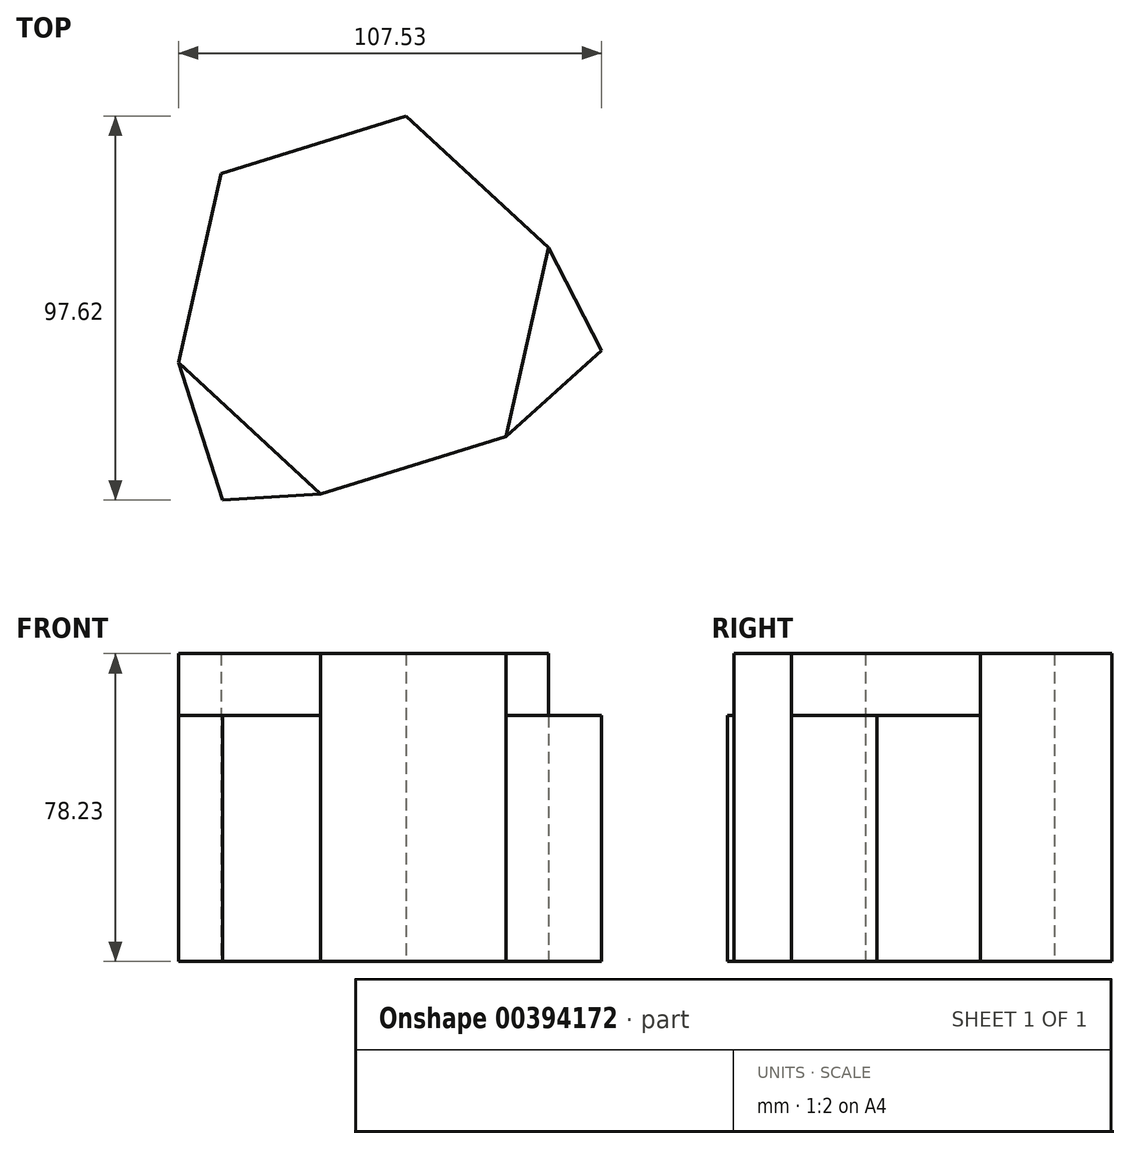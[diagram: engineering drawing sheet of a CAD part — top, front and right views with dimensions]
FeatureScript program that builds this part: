
annotation { "Feature Type Name" : "Feature", "Feature Type Description" : "" }
export const myFeature = defineFeature(function(context is Context, id is Id, definition is map)
    precondition{}
    {
        {
            var Q0;
            Q0=qCreatedBy(makeId("Top.planeOp"),FACE);
            var sketch = newSketch(context, id + "F0", { "sketchPlane" : qUnion([Q0])});
            skCircle(sketch, "E0.cCircle", {"center": v(0, 0) * mm, "radius": 42.64 * mm, "construction": true});
            skLineSegment(sketch, "E0.0", {"start": v(-47.01, -14.63) * mm, "end": v(-36.18, 33.4) * mm});
            skLineSegment(sketch, "E0.1", {"start": v(-36.18, 33.4) * mm, "end": v(10.83, 48.03) * mm});
            skLineSegment(sketch, "E0.2", {"start": v(10.83, 48.03) * mm, "end": v(47.01, 14.63) * mm});
            skLineSegment(sketch, "E0.3", {"start": v(47.01, 14.63) * mm, "end": v(36.18, -33.4) * mm});
            skLineSegment(sketch, "E0.4", {"start": v(36.18, -33.4) * mm, "end": v(-10.83, -48.03) * mm});
            skLineSegment(sketch, "E0.5", {"start": v(-10.83, -48.03) * mm, "end": v(-47.01, -14.63) * mm});
            skPoint(sketch, "E0.0.midPoint", {"position": v(-41.6, 9.38) * mm});
            skLineSegment(sketch, "E1", {"start": v(-47.01, -14.63) * mm, "end": v(-35.83, -49.59) * mm});
            skLineSegment(sketch, "E2", {"start": v(-35.83, -49.59) * mm, "end": v(-10.83, -48.03) * mm});
            skLineSegment(sketch, "E3", {"start": v(36.18, -33.4) * mm, "end": v(60.52, -11.59) * mm});
            skLineSegment(sketch, "E4", {"start": v(60.52, -11.59) * mm, "end": v(47.01, 14.63) * mm});
            skSolve(sketch);
        }
        {
            var Q0;
            Q0=makeQuery(id+"F0.imprint","IMPRINT",FACE,{"disambiguationData":[TD([[makeQuery(id+"F0.imprint","IMPRINT",EDGE,{"derivedFrom":sQuery(id+"F0.wireOp",EDGE,"E0.0")}),-1.0]])]});
            extrude(context, id + "F1", {"entities" : qUnion([Q0]), "depth" : 78.23 * mm});
        }
        {
            var Q0;
            Q0=makeQuery(id+"F0.imprint","IMPRINT",FACE,{"disambiguationData":[TD([[makeQuery(id+"F0.imprint","IMPRINT",EDGE,{"derivedFrom":sQuery(id+"F0.wireOp",EDGE,"E0.5")}),1.0]])]});
            extrude(context, id + "F2", {"entities" : qUnion([Q0]), "operationType" : NewBodyOperationType.ADD, "depth" : 62.48 * mm});
        }
        {
            var Q0;
            Q0=makeQuery(id+"F0.imprint","IMPRINT",FACE,{"disambiguationData":[TD([[makeQuery(id+"F0.imprint","IMPRINT",EDGE,{"derivedFrom":sQuery(id+"F0.wireOp",EDGE,"E0.3")}),1.0]])]});
            extrude(context, id + "F3", {"entities" : qUnion([Q0]), "operationType" : NewBodyOperationType.ADD, "depth" : 62.48 * mm});
        }
    });
